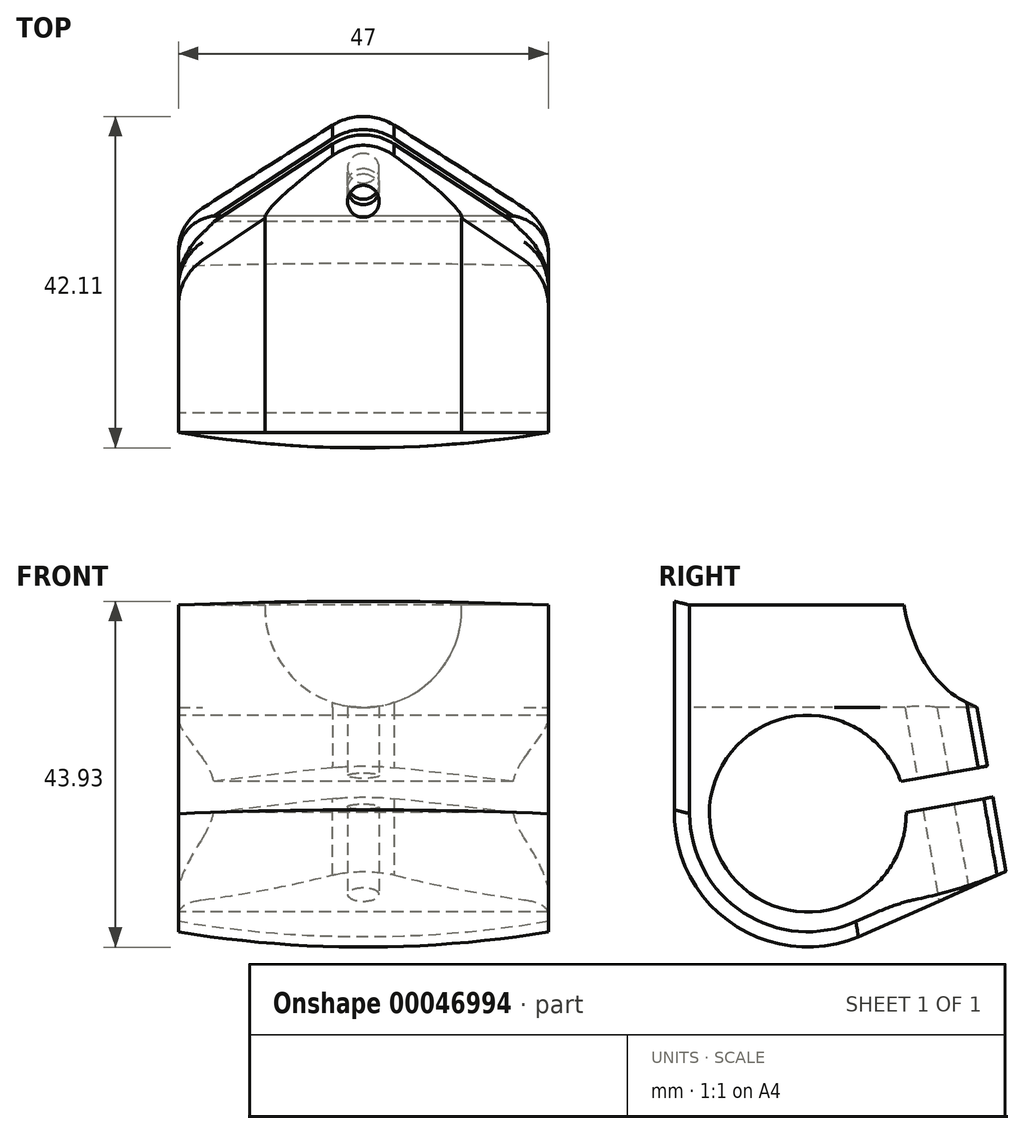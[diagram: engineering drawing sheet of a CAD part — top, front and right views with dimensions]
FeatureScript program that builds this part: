
annotation { "Feature Type Name" : "Feature", "Feature Type Description" : "" }
export const myFeature = defineFeature(function(context is Context, id is Id, definition is map)
    precondition{}
    {
        {
            var Q0;
            Q0=qCreatedBy(makeId("Right.planeOp"),FACE);
            var sketch = newSketch(context, id + "F0", { "sketchPlane" : qUnion([Q0])});
            skCircle(sketch, "E0", {"center": v(0, 0) * mm, "radius": 12.5 * mm});
            skCircle(sketch, "E1", {"center": v(0, 0) * mm, "radius": 15 * mm});
            skLineSegment(sketch, "E2", {"start": v(51.64, 13.5) * mm, "end": v(-46.63, 13.5) * mm, "construction": true});
            skLineSegment(sketch, "E3", {"start": v(51.63, 15) * mm, "end": v(-45.98, 15) * mm, "construction": true});
            skLineSegment(sketch, "E4", {"start": v(0, 0) * mm, "end": v(31.28, 5.52) * mm, "construction": true});
            skLineSegment(sketch, "E5", {"start": v(6.1, -13.7) * mm, "end": v(24.81, -5.37) * mm});
            skLineSegment(sketch, "E6", {"start": v(28.44, -25.97) * mm, "end": v(23.5, 2.11) * mm});
            skLineSegment(sketch, "E7", {"start": v(23.5, 2.11) * mm, "end": v(12.5, 0.17) * mm});
            skLineSegment(sketch, "E8.MirrorCS", {"start": v(22.8, 6.05) * mm, "end": v(11.8, 4.11) * mm});
            skLineSegment(sketch, "E9", {"start": v(23.14, 4.08) * mm, "end": v(23.5, 2.11) * mm});
            skPoint(sketch, "E10.orphan", {"position": v(14.99, 0.61) * mm});
            skPoint(sketch, "E11.orphan", {"position": v(14.3, 4.55) * mm});
            skLineSegment(sketch, "E12", {"start": v(22.8, 6.05) * mm, "end": v(21.48, 13.5) * mm});
            skLineSegment(sketch, "E13", {"start": v(19.19, 26.5) * mm, "end": v(-15, 26.5) * mm});
            skLineSegment(sketch, "E14", {"start": v(-15, 26.5) * mm, "end": v(-15, 0) * mm});
            skLineSegment(sketch, "E15", {"start": v(23.14, 4.08) * mm, "end": v(22.8, 6.05) * mm});
            skLineSegment(sketch, "E16", {"start": v(21.48, 13.5) * mm, "end": v(19.19, 26.5) * mm});
            skArc(sketch, "E17", {"start": v(21.11, 17.74) * mm, "mid": v(21.2, 15.61) * mm, "end": v(21.48, 13.5) * mm});
            skLineSegment(sketch, "E18", {"start": v(21.11, 17.74) * mm, "end": v(21.11, 26.85) * mm});
            skLineSegment(sketch, "E19", {"start": v(0, 0) * mm, "end": v(0, 26.5) * mm, "construction": true});
            skPoint(sketch, "E20.orphan", {"position": v(-21.48, 13.5) * mm});
            skSolve(sketch);
        }
        {
            var Q0;
            {var subQ0=sQuery(id+"F0.wireOp",EDGE,"E12");Q0=makeQuery(id+"F0.imprint","IMPRINT",FACE,{"disambiguationData":[TD([[makeQuery(id+"F0.imprint","IMPRINT",EDGE,{"derivedFrom":subQ0}),1.0]])]});}
            var Q1;
            {var subQ2=sQuery(id+"F0.wireOp",EDGE,"E7");var subQ7=sQuery(id+"F0.wireOp",EDGE,"E0");var subQ8=makeQuery(id+"F0.imprint","INTERSECT",VERTEX,{"derivedFrom":[subQ7,subQ2]});Q1=makeQuery(id+"F0.imprint","IMPRINT",FACE,{"disambiguationData":[TD([[makeQuery(id+"F0.imprint","IMPRINT",EDGE,{"disambiguationData":[TD([[subQ8,1.0]])],"derivedFrom":subQ7}),-1.0]])]});}
            var Q2;
            {var subQ0=sQuery(id+"F0.wireOp",EDGE,"E5");Q2=makeQuery(id+"F0.imprint","IMPRINT",FACE,{"disambiguationData":[TD([[makeQuery(id+"F0.imprint","IMPRINT",EDGE,{"derivedFrom":subQ0}),1.0]])]});}
            extrude(context, id + "F1", {"entities" : qUnion([Q0, Q1, Q2]), "endBound" : BoundingType.SYMMETRIC, "depth" : 47 * mm});
        }
        {
            var Q0;
            Q0=qCreatedBy(makeId("Right.planeOp"),FACE);
            var sketch = newSketch(context, id + "F2", { "sketchPlane" : qUnion([Q0])});
            skCircle(sketch, "E21", {"center": v(0, 0) * mm, "radius": 12.5 * mm});
            skCircle(sketch, "E22", {"center": v(0, 0) * mm, "radius": 15 * mm});
            skLineSegment(sketch, "E23", {"start": v(51.64, 13.5) * mm, "end": v(-46.63, 13.5) * mm, "construction": true});
            skLineSegment(sketch, "E24", {"start": v(51.63, 15) * mm, "end": v(-45.98, 15) * mm, "construction": true});
            skLineSegment(sketch, "E25", {"start": v(0, 0) * mm, "end": v(31.28, 5.52) * mm, "construction": true});
            skLineSegment(sketch, "E26", {"start": v(6.1, -13.7) * mm, "end": v(24.81, -5.37) * mm});
            skLineSegment(sketch, "E27", {"start": v(24.81, -5.37) * mm, "end": v(23.5, 2.11) * mm});
            skLineSegment(sketch, "E28", {"start": v(23.5, 2.11) * mm, "end": v(12.5, 0.17) * mm});
            skLineSegment(sketch, "E29.MirrorCS", {"start": v(22.8, 6.05) * mm, "end": v(11.8, 4.11) * mm});
            skLineSegment(sketch, "E30", {"start": v(22.8, 6.05) * mm, "end": v(23.5, 2.11) * mm, "construction": true});
            skPoint(sketch, "E31.orphan", {"position": v(14.99, 0.61) * mm});
            skPoint(sketch, "E32.orphan", {"position": v(14.3, 4.55) * mm});
            skLineSegment(sketch, "E33", {"start": v(22.8, 6.05) * mm, "end": v(19.19, 26.5) * mm});
            skLineSegment(sketch, "E34", {"start": v(20.54, 18.85) * mm, "end": v(-2.6, 14.77) * mm});
            skLineSegment(sketch, "E35", {"start": v(19.19, 26.5) * mm, "end": v(-15, 26.5) * mm});
            skLineSegment(sketch, "E36", {"start": v(-15, 26.5) * mm, "end": v(-15, 0) * mm});
            skLineSegment(sketch, "E37", {"start": v(-17, -10.25) * mm, "end": v(-17, 26.5) * mm});
            skSolve(sketch);
        }
        {
            var Q0;
            Q0=makeQuery(id+"F1.opExtrude","SWEPT_FACE",FACE,{"disambiguationData":[OSD([sQuery(id+"F0.wireOp",EDGE,"E6")])]});
            var sketch = newSketch(context, id + "F3", { "sketchPlane" : qUnion([Q0])});
            skArc(sketch, "E38", {"start": v(-23.5, -9.6) * mm, "mid": v(0, -11.6) * mm, "end": v(23.5, -9.6) * mm});
            skSolve(sketch);
        }
        {
            var Q0;
            Q0=makeQuery(id+"F3.imprint","IMPRINT",FACE,{"disambiguationData":[TD([[makeQuery(id+"F3.imprint","IMPRINT",EDGE,{"derivedFrom":sQuery(id+"F3.wireOp",EDGE,"E38")}),1.0]])]});
            var Q1;
            Q1=makeQuery(id+"F1.opExtrude","CAP_EDGE",EDGE,{"disambiguationData":[OSD([sQuery(id+"F0.wireOp",EDGE,"E5")])],"isStart":false});
            var Q2;
            Q2=makeQuery(id+"F1.opExtrude","CAP_EDGE",EDGE,{"disambiguationData":[OSD([sQuery(id+"F0.wireOp",EDGE,"E1")])],"isStart":false});
            sweep(context, id + "F4", {"operationType" : NewBodyOperationType.ADD, "profiles" : qUnion([Q0]), "path" : qUnion([Q1, Q2])});
        }
        {
            var Q0;
            Q0=qCreatedBy(makeId("Front.planeOp"),FACE);
            var sketch = newSketch(context, id + "F5", { "sketchPlane" : qUnion([Q0])});
            skCircle(sketch, "E39", {"center": v(0, 26) * mm, "radius": 12.5 * mm});
            skSolve(sketch);
        }
        {
            var Q0;
            Q0=makeQuery(id+"F5.imprint","IMPRINT",FACE,{"disambiguationData":[TD([[makeQuery(id+"F5.imprint","IMPRINT",EDGE,{"derivedFrom":sQuery(id+"F5.wireOp",EDGE,"E39")}),1.0]])]});
            extrude(context, id + "F6", {"entities" : qUnion([Q0]), "operationType" : NewBodyOperationType.REMOVE, "endBound" : BoundingType.THROUGH_ALL, "oppositeDirection" : true, "depth" : 25 * mm, "hasSecondDirection" : true, "secondDirectionBound" : SecondDirectionBoundingType.THROUGH_ALL, "secondDirectionOppositeDirection" : false, "secondDirectionDepth" : 25 * mm});
        }
        {
            var Q0;
            Q0=makeQuery(id+"F1.opExtrude","SWEPT_FACE",FACE,{"disambiguationData":[OSD([sQuery(id+"F0.wireOp",EDGE,"E8.MirrorCS")])]});
            cPlane(context, id + "F7", {"entities" : qUnion([Q0]), "cplaneType" : CPlaneType.OFFSET, "offset" : 30 * mm, "width" : 150 * mm, "height" : 150 * mm});
        }
        {
            var Q0;
            Q0=qCreatedBy(id+"F7.planeOp",FACE);
            var sketch = newSketch(context, id + "F8", { "sketchPlane" : qUnion([Q0])});
            skCircle(sketch, "E40", {"center": v(0, -16.5) * mm, "radius": 7 * mm});
            skCircle(sketch, "E41", {"center": v(0, -16.5) * mm, "radius": 5 * mm});
            skCircle(sketch, "E42", {"center": v(0, -16.5) * mm, "radius": 2 * mm});
            skLineSegment(sketch, "E43", {"start": v(-23.5, -23.5) * mm, "end": v(-23.5, 18.65) * mm});
            skLineSegment(sketch, "E44", {"start": v(23.5, -23.5) * mm, "end": v(23.5, 18.65) * mm});
            skLineSegment(sketch, "E45", {"start": v(-23.5, -23.5) * mm, "end": v(23.5, -23.5) * mm});
            skLineSegment(sketch, "E46", {"start": v(3.5, -22.56) * mm, "end": v(23.5, -11.02) * mm});
            skLineSegment(sketch, "E47", {"start": v(-3.5, -22.56) * mm, "end": v(-23.5, -11.02) * mm});
            skSolve(sketch);
        }
        {
            var Q0;
            {var subQ0=sQuery(id+"F8.wireOp",EDGE,"E47");Q0=makeQuery(id+"F8.imprint","IMPRINT",FACE,{"disambiguationData":[TD([[makeQuery(id+"F8.imprint","IMPRINT",EDGE,{"derivedFrom":subQ0}),1.0]])]});}
            var Q1;
            {var subQ0=sQuery(id+"F8.wireOp",EDGE,"E46");Q1=makeQuery(id+"F8.imprint","IMPRINT",FACE,{"disambiguationData":[TD([[makeQuery(id+"F8.imprint","IMPRINT",EDGE,{"derivedFrom":subQ0}),-1.0]])]});}
            var Q2;
            Q2=makeQuery(id+"F8.imprint","IMPRINT",FACE,{"disambiguationData":[TD([[makeQuery(id+"F8.imprint","IMPRINT",EDGE,{"derivedFrom":sQuery(id+"F8.wireOp",EDGE,"E42")}),1.0]])]});
            var Q3;
            {var subQ1=sQuery(id+"F0.wireOp",EDGE,"E14");var subQ2=sQuery(id+"F0.wireOp",EDGE,"E13");var subQ3=sQuery(id+"F0.wireOp",EDGE,"E6");var subQ4=sQuery(id+"F0.wireOp",EDGE,"E5");var subQ5=sQuery(id+"F0.wireOp",EDGE,"E12");Q3=makeQuery(id+"F6.boolean.opBoolean","SPLIT",FACE,{"disambiguationData":[TD([makeQuery(id+"F1.opExtrude","CAP_FACE",FACE,{"disambiguationData":[OSD([sQuery(id+"F0.wireOp",EDGE,"E0"),sQuery(id+"F0.wireOp",EDGE,"E1"),subQ4,subQ3,sQuery(id+"F0.wireOp",EDGE,"E7"),sQuery(id+"F0.wireOp",EDGE,"E8.MirrorCS"),subQ5,subQ2,subQ1])],"isStart":true})])],"derivedFrom":makeQuery(id+"F1.opExtrude","SWEPT_FACE",FACE,{"disambiguationData":[OSD([subQ2])]})});}
            extrude(context, id + "F9", {"entities" : qUnion([Q0, Q1, Q2]), "operationType" : NewBodyOperationType.REMOVE, "endBound" : BoundingType.UP_TO_SURFACE, "oppositeDirection" : true, "endBoundEntityFace" : qUnion([Q3]), "depth" : 25 * mm});
        }
        {
            var Q0;
            {var subQ1=sQuery(id+"F0.wireOp",EDGE,"E14");var subQ2=sQuery(id+"F0.wireOp",EDGE,"E13");var subQ3=sQuery(id+"F0.wireOp",EDGE,"E6");var subQ4=sQuery(id+"F0.wireOp",EDGE,"E5");var subQ5=sQuery(id+"F0.wireOp",EDGE,"E16");var subQ6=sQuery(id+"F0.wireOp",EDGE,"E12");Q0=makeQuery(id+"F6.boolean.opBoolean","SPLIT",FACE,{"disambiguationData":[TD([makeQuery(id+"F1.opExtrude","CAP_FACE",FACE,{"disambiguationData":[OSD([sQuery(id+"F0.wireOp",EDGE,"E0"),sQuery(id+"F0.wireOp",EDGE,"E1"),subQ4,subQ3,sQuery(id+"F0.wireOp",EDGE,"E7"),sQuery(id+"F0.wireOp",EDGE,"E8.MirrorCS"),subQ6,subQ2,subQ1,subQ5])],"isStart":true})])],"derivedFrom":makeQuery(id+"F1.opExtrude","SWEPT_FACE",FACE,{"disambiguationData":[OSD([subQ2])]})});}
            var sketch = newSketch(context, id + "F10", { "sketchPlane" : qUnion([Q0])});
            skArc(sketch, "E48", {"start": v(-9.5, 1.1) * mm, "mid": v(-16.5, 8.1) * mm, "end": v(-23.5, 1.1) * mm});
            skLineSegment(sketch, "E49", {"start": v(-20.4, 6.9) * mm, "end": v(-3.9, 18) * mm});
            skLineSegment(sketch, "E50", {"start": v(23.5, 1.1) * mm, "end": v(-23.5, 1.1) * mm, "construction": true});
            skLineSegment(sketch, "E51", {"start": v(0, -21.4) * mm, "end": v(0, 26.51) * mm, "construction": true});
            skArc(sketch, "E52.MirrorC", {"start": v(9.5, 1.1) * mm, "mid": v(16.5, 8.1) * mm, "end": v(23.5, 1.1) * mm});
            skLineSegment(sketch, "E53.MirrorCS", {"start": v(20.4, 6.9) * mm, "end": v(3.9, 18) * mm});
            skCircle(sketch, "E54", {"center": v(0, 12.19) * mm, "radius": 7 * mm});
            skLineSegment(sketch, "E55", {"start": v(-23.5, 19.19) * mm, "end": v(23.5, 19.19) * mm});
            skLineSegment(sketch, "E56", {"start": v(-23.5, 19.19) * mm, "end": v(-23.5, 1.1) * mm});
            skLineSegment(sketch, "E57", {"start": v(23.5, 1.1) * mm, "end": v(23.5, 19.19) * mm});
            skLineSegment(sketch, "E58", {"start": v(-26.8, 1.1) * mm, "end": v(29.8, 1.1) * mm, "construction": true});
            skArc(sketch, "E59.MirrorCS", {"start": v(-9.5, 1.1) * mm, "mid": v(-16.5, -5.9) * mm, "end": v(-23.5, 1.1) * mm});
            skLineSegment(sketch, "E60.MirrorCS", {"start": v(-20.4, -4.71) * mm, "end": v(-3.9, -15.8) * mm});
            skLineSegment(sketch, "E61.MirrorCS", {"start": v(20.4, -4.71) * mm, "end": v(3.9, -15.8) * mm});
            skArc(sketch, "E62.MirrorCS", {"start": v(9.5, 1.1) * mm, "mid": v(16.5, -5.9) * mm, "end": v(23.5, 1.1) * mm});
            skLineSegment(sketch, "E63.MirrorCS", {"start": v(23.5, 1.1) * mm, "end": v(23.5, -17) * mm});
            skLineSegment(sketch, "E64.MirrorCS", {"start": v(-23.5, -17) * mm, "end": v(23.5, -17) * mm});
            skLineSegment(sketch, "E65.MirrorCS", {"start": v(-23.5, -17) * mm, "end": v(-23.5, 1.1) * mm});
            skArc(sketch, "E66", {"start": v(0, -17) * mm, "mid": v(-5.73, -14.03) * mm, "end": v(-6.59, -7.63) * mm});
            skArc(sketch, "E67", {"start": v(-6.59, -7.63) * mm, "mid": v(5.73, -5.97) * mm, "end": v(0, -17) * mm});
            skSolve(sketch);
        }
        {
            var Q0;
            {var subQ3=sQuery(id+"F10.wireOp",EDGE,"E48");var subQ5=sQuery(id+"F10.wireOp",EDGE,"E49");var subQ6=makeQuery(id+"F10.imprint","INTERSECT",VERTEX,{"derivedFrom":[subQ3,subQ5]});Q0=makeQuery(id+"F10.imprint","IMPRINT",FACE,{"disambiguationData":[TD([[makeQuery(id+"F10.imprint","IMPRINT",EDGE,{"disambiguationData":[TD([[subQ6,-1.0]])],"derivedFrom":subQ3}),-1.0]])]});}
            var Q1;
            {var subQ0=sQuery(id+"F10.wireOp",EDGE,"E54");var subQ1=sQuery(id+"F10.wireOp",EDGE,"E49");var subQ2=makeQuery(id+"F10.imprint","INTERSECT",VERTEX,{"derivedFrom":[subQ1,subQ0]});Q1=makeQuery(id+"F10.imprint","IMPRINT",FACE,{"disambiguationData":[TD([[makeQuery(id+"F10.imprint","IMPRINT",EDGE,{"disambiguationData":[TD([[subQ2,1.0]])],"derivedFrom":subQ0}),-1.0]])]});}
            var Q2;
            Q2=sQuery(id+"F0.wireOp",EDGE,"E16");
            var Q3;
            Q3=sQuery(id+"F0.wireOp",EDGE,"E12");
            var Q4;
            Q4=sQuery(id+"F0.wireOp",EDGE,"E15");
            var Q5;
            Q5=sQuery(id+"F0.wireOp",EDGE,"E9");
            var Q6;
            Q6=sQuery(id+"F0.wireOp",EDGE,"E6");
            sweep(context, id + "F11", {"operationType" : NewBodyOperationType.REMOVE, "profiles" : qUnion([Q0, Q1]), "path" : qUnion([Q2, Q3, Q4, Q5, Q6])});
        }
        {
            var Q0;
            {var subQ5=sQuery(id+"F10.wireOp",EDGE,"E53.MirrorCS");Q0=makeQuery(id+"F10.imprint","IMPRINT",FACE,{"disambiguationData":[TD([[makeQuery(id+"F10.imprint","IMPRINT",EDGE,{"derivedFrom":subQ5}),-1.0]])]});}
            var Q1;
            Q1=sQuery(id+"F0.wireOp",EDGE,"E16");
            var Q2;
            Q2=sQuery(id+"F0.wireOp",EDGE,"E12");
            var Q3;
            Q3=sQuery(id+"F0.wireOp",EDGE,"E9");
            var Q4;
            Q4=sQuery(id+"F0.wireOp",EDGE,"E15");
            var Q5;
            Q5=sQuery(id+"F0.wireOp",EDGE,"E6");
            sweep(context, id + "F12", {"operationType" : NewBodyOperationType.REMOVE, "profiles" : qUnion([Q0]), "path" : qUnion([Q1, Q2, Q3, Q4, Q5])});
        }
        {
            var Q0;
            Q0=makeQuery(id+"F4.opSweep","CAP_FACE",FACE,{"disambiguationData":[OSD([sQuery(id+"F0.wireOp",EDGE,"E1"),sQuery(id+"F0.wireOp",EDGE,"E5"),sQuery(id+"F0.wireOp",EDGE,"E6"),sQuery(id+"F0.wireOp",EDGE,"E14"),sQuery(id+"F3.wireOp",EDGE,"E38")])],"isStart":false});
            var sketch = newSketch(context, id + "F13", { "sketchPlane" : qUnion([Q0])});
            skLineSegment(sketch, "E68", {"start": v(23.5, -16.55) * mm, "end": v(-23.5, -16.55) * mm});
            skLineSegment(sketch, "E69", {"start": v(23.5, -14.55) * mm, "end": v(23.5, -16.55) * mm});
            skLineSegment(sketch, "E70", {"start": v(-23.5, -14.55) * mm, "end": v(-23.5, -16.55) * mm});
            skSolve(sketch);
        }
        {
            var Q0;
            Q0=makeQuery(id+"F4.opSweep","CAP_FACE",FACE,{"disambiguationData":[OSD([sQuery(id+"F0.wireOp",EDGE,"E1"),sQuery(id+"F0.wireOp",EDGE,"E5"),sQuery(id+"F0.wireOp",EDGE,"E6"),sQuery(id+"F0.wireOp",EDGE,"E14"),sQuery(id+"F3.wireOp",EDGE,"E38")])],"isStart":false});
            var Q1;
            Q1=makeQuery(id+"F1.opExtrude","CAP_EDGE",EDGE,{"disambiguationData":[OSD([sQuery(id+"F0.wireOp",EDGE,"E14")])],"isStart":true});
            sweep(context, id + "F14", {"operationType" : NewBodyOperationType.ADD, "profiles" : qUnion([Q0]), "path" : qUnion([Q1])});
        }
        {
            var Q0;
            Q0=sQuery(id+"F13.wireOp",VERTEX,"E69.start");
            var Q1;
            Q1=sQuery(id+"F13.wireOp",VERTEX,"E69.end");
            var Q2;
            Q2=sQuery(id+"F10.wireOp",VERTEX,"E64.MirrorCS.end");
            cPlane(context, id + "F15", {"entities" : qUnion([Q0, Q1, Q2]), "cplaneType" : CPlaneType.THREE_POINT, "offset" : 150 * mm, "width" : 150 * mm, "height" : 150 * mm});
        }
        {
            var Q0;
            Q0=qCreatedBy(id+"F15.planeOp",FACE);
            var sketch = newSketch(context, id + "F16", { "sketchPlane" : qUnion([Q0])});
            skLineSegment(sketch, "E71", {"start": v(-17, 26.5) * mm, "end": v(-16.94, 0.48) * mm});
            skArc(sketch, "E72", {"start": v(1.1, 14.96) * mm, "mid": v(-10.21, 10.99) * mm, "end": v(-15, 0) * mm});
            skLineSegment(sketch, "E73", {"start": v(1.1, 26.5) * mm, "end": v(1.1, 14.96) * mm});
            skSolve(sketch);
        }
        {
            var Q0;
            Q0=sQuery(id+"F10.wireOp",VERTEX,"E67.end");
            var Q1;
            Q1=sQuery(id+"F16.wireOp",VERTEX,"E71.start");
            var Q2;
            Q2=sQuery(id+"F16.wireOp",VERTEX,"E71.end");
            cPlane(context, id + "F17", {"entities" : qUnion([Q0, Q1, Q2]), "cplaneType" : CPlaneType.THREE_POINT, "offset" : 150 * mm, "width" : 150 * mm, "height" : 150 * mm});
        }
    });
